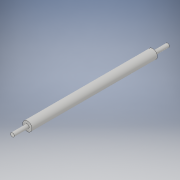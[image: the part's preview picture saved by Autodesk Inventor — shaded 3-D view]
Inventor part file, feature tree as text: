
AUTODESK INVENTOR PART (.ipt)
format: ipt  version: 2018 (Build 220112000, 112)  size: 101,376 bytes
history: native  units: in
note: dims shown in document units (in); Inventor stores cm internally (conversion verified against a paired STEP export)
features: extrude x3, sketch x3
ambient origin geometry x8: Origin, YZ Plane, XZ Plane, XY Plane, X Axis, Y Axis, Z Axis, Center Point
bodies: Solid1 (feature_tree)
feature tree (6):
  extrude  "Extrusion1"  Depth=3.3071in TaperAngle=0.0deg
  extrude  "Extrusion2"  Depth=0.3937in TaperAngle=0.0deg
  extrude  "Extrusion3"  Depth=0.3937in TaperAngle=0.0deg
  sketch  "Sketch1"  dims[d0=0.2441in d1=3.3071in d2=0.0in]
  sketch  "Sketch2"  dims[d3=0.0984in d4=0.3937in d5=0.0in]
  sketch  "Sketch3"  dims[d6=0.0984in d7=0.3937in d8=0.0in]
